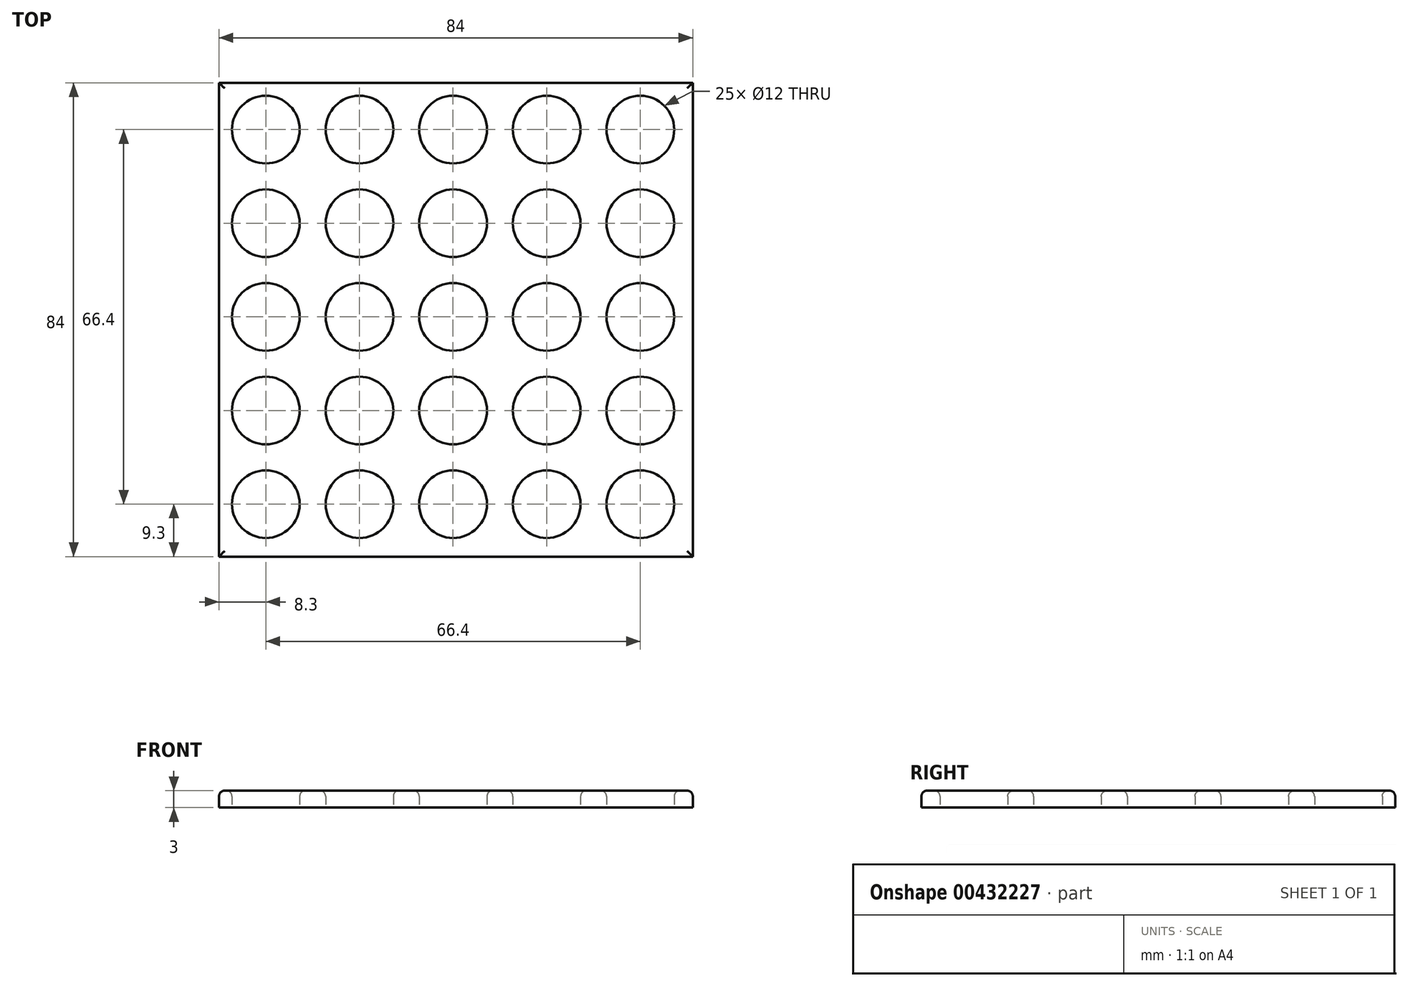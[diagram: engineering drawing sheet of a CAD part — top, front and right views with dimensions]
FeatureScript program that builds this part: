
annotation { "Feature Type Name" : "Feature", "Feature Type Description" : "" }
export const myFeature = defineFeature(function(context is Context, id is Id, definition is map)
    precondition{}
    {
        {
            var Q0;
            Q0=qCreatedBy(makeId("Top.planeOp"),FACE);
            var sketch = newSketch(context, id + "F0", { "sketchPlane" : qUnion([Q0])});
            skLineSegment(sketch, "E0.bottom", {"start": v(42, 42) * mm, "end": v(-42, 42) * mm});
            skLineSegment(sketch, "E0.top", {"start": v(42, -42) * mm, "end": v(-42, -42) * mm});
            skLineSegment(sketch, "E0.left", {"start": v(42, 42) * mm, "end": v(42, -42) * mm});
            skLineSegment(sketch, "E0.right", {"start": v(-42, 42) * mm, "end": v(-42, -42) * mm});
            skPoint(sketch, "E0.middle", {"position": v(0, 0) * mm});
            skCircle(sketch, "E1", {"center": v(-33.7, 33.7) * mm, "radius": 6 * mm});
            skCircle(sketch, "E2.0.1.0", {"center": v(-33.7, 17.1) * mm, "radius": 6 * mm});
            skCircle(sketch, "E2.0.2.0", {"center": v(-33.7, 0.5) * mm, "radius": 6 * mm});
            skCircle(sketch, "E2.0.3.0", {"center": v(-33.7, -16.1) * mm, "radius": 6 * mm});
            skCircle(sketch, "E2.0.4.0", {"center": v(-33.7, -32.7) * mm, "radius": 6 * mm});
            skCircle(sketch, "E2.1.0.0", {"center": v(-17.1, 33.7) * mm, "radius": 6 * mm});
            skCircle(sketch, "E2.1.1.0", {"center": v(-17.1, 17.1) * mm, "radius": 6 * mm});
            skCircle(sketch, "E2.1.2.0", {"center": v(-17.1, 0.5) * mm, "radius": 6 * mm});
            skCircle(sketch, "E2.1.3.0", {"center": v(-17.1, -16.1) * mm, "radius": 6 * mm});
            skCircle(sketch, "E2.1.4.0", {"center": v(-17.1, -32.7) * mm, "radius": 6 * mm});
            skCircle(sketch, "E2.2.0.0", {"center": v(-0.5, 33.7) * mm, "radius": 6 * mm});
            skCircle(sketch, "E2.2.1.0", {"center": v(-0.5, 17.1) * mm, "radius": 6 * mm});
            skCircle(sketch, "E2.2.2.0", {"center": v(-0.5, 0.5) * mm, "radius": 6 * mm});
            skCircle(sketch, "E2.2.3.0", {"center": v(-0.5, -16.1) * mm, "radius": 6 * mm});
            skCircle(sketch, "E2.2.4.0", {"center": v(-0.5, -32.7) * mm, "radius": 6 * mm});
            skCircle(sketch, "E2.3.0.0", {"center": v(16.1, 33.7) * mm, "radius": 6 * mm});
            skCircle(sketch, "E2.3.1.0", {"center": v(16.1, 17.1) * mm, "radius": 6 * mm});
            skCircle(sketch, "E2.3.2.0", {"center": v(16.1, 0.5) * mm, "radius": 6 * mm});
            skCircle(sketch, "E2.3.3.0", {"center": v(16.1, -16.1) * mm, "radius": 6 * mm});
            skCircle(sketch, "E2.3.4.0", {"center": v(16.1, -32.7) * mm, "radius": 6 * mm});
            skCircle(sketch, "E2.4.0.0", {"center": v(32.7, 33.7) * mm, "radius": 6 * mm});
            skCircle(sketch, "E2.4.1.0", {"center": v(32.7, 17.1) * mm, "radius": 6 * mm});
            skCircle(sketch, "E2.4.2.0", {"center": v(32.7, 0.5) * mm, "radius": 6 * mm});
            skCircle(sketch, "E2.4.3.0", {"center": v(32.7, -16.1) * mm, "radius": 6 * mm});
            skCircle(sketch, "E2.4.4.0", {"center": v(32.7, -32.7) * mm, "radius": 6 * mm});
            skLineSegment(sketch, "E2.direction1", {"start": v(-33.7, 33.7) * mm, "end": v(-17.1, 33.7) * mm, "construction": true});
            skLineSegment(sketch, "E2.direction2", {"start": v(-33.7, 33.7) * mm, "end": v(-33.7, 17.1) * mm, "construction": true});
            skSolve(sketch);
        }
        {
            var Q0;
            Q0 = qSketchRegion(id + "F0", true);
            extrude(context, id + "F1", {"entities" : qUnion([Q0]), "depth" : 3 * mm});
        }
        {
            var Q0;
            Q0=makeQuery(id+"F1.opExtrude","CAP_FACE",FACE,{"disambiguationData":[OSD([sQuery(id+"F0.wireOp",EDGE,"E0.bottom"),sQuery(id+"F0.wireOp",EDGE,"E0.top"),sQuery(id+"F0.wireOp",EDGE,"E0.left"),sQuery(id+"F0.wireOp",EDGE,"E0.right"),sQuery(id+"F0.wireOp",EDGE,"E1"),sQuery(id+"F0.wireOp",EDGE,"E2.0.1.0"),sQuery(id+"F0.wireOp",EDGE,"E2.0.2.0"),sQuery(id+"F0.wireOp",EDGE,"E2.0.3.0"),sQuery(id+"F0.wireOp",EDGE,"E2.0.4.0"),sQuery(id+"F0.wireOp",EDGE,"E2.1.0.0"),sQuery(id+"F0.wireOp",EDGE,"E2.1.1.0"),sQuery(id+"F0.wireOp",EDGE,"E2.1.2.0"),sQuery(id+"F0.wireOp",EDGE,"E2.1.3.0"),sQuery(id+"F0.wireOp",EDGE,"E2.1.4.0"),sQuery(id+"F0.wireOp",EDGE,"E2.2.0.0"),sQuery(id+"F0.wireOp",EDGE,"E2.2.1.0"),sQuery(id+"F0.wireOp",EDGE,"E2.2.2.0"),sQuery(id+"F0.wireOp",EDGE,"E2.2.3.0"),sQuery(id+"F0.wireOp",EDGE,"E2.2.4.0"),sQuery(id+"F0.wireOp",EDGE,"E2.3.0.0"),sQuery(id+"F0.wireOp",EDGE,"E2.3.1.0"),sQuery(id+"F0.wireOp",EDGE,"E2.3.2.0"),sQuery(id+"F0.wireOp",EDGE,"E2.3.3.0"),sQuery(id+"F0.wireOp",EDGE,"E2.3.4.0"),sQuery(id+"F0.wireOp",EDGE,"E2.4.0.0"),sQuery(id+"F0.wireOp",EDGE,"E2.4.1.0"),sQuery(id+"F0.wireOp",EDGE,"E2.4.2.0"),sQuery(id+"F0.wireOp",EDGE,"E2.4.3.0"),sQuery(id+"F0.wireOp",EDGE,"E2.4.4.0")])],"isStart":false});
            fillet(context, id + "F2", {"entities" : qUnion([Q0]), "radius" : 1 * mm, "tangentPropagation" : true, "allowEdgeOverflow" : false});
        }
    });
